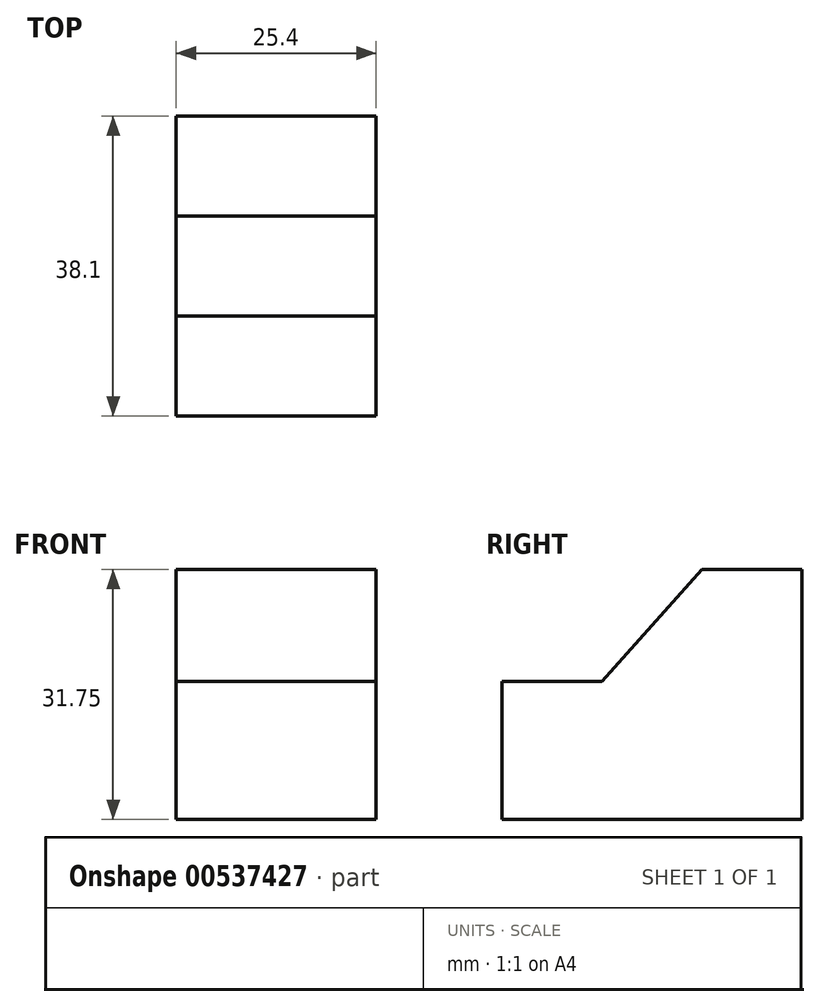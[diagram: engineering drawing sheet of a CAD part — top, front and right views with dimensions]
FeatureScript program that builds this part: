
annotation { "Feature Type Name" : "Feature", "Feature Type Description" : "" }
export const myFeature = defineFeature(function(context is Context, id is Id, definition is map)
    precondition{}
    {
        {
            var Q0;
            Q0=qCreatedBy(makeId("Top.planeOp"),FACE);
            var sketch = newSketch(context, id + "F0", { "sketchPlane" : qUnion([Q0])});
            skLineSegment(sketch, "E0", {"start": v(0, 0) * mm, "end": v(0, 38.1) * mm});
            skLineSegment(sketch, "E1", {"start": v(0, 38.1) * mm, "end": v(25.4, 38.1) * mm});
            skLineSegment(sketch, "E2", {"start": v(25.4, 38.1) * mm, "end": v(25.4, 0) * mm});
            skLineSegment(sketch, "E3", {"start": v(25.4, 0) * mm, "end": v(0, 0) * mm});
            skSolve(sketch);
        }
        {
            var Q0;
            Q0 = qSketchRegion(id + "F0", true);
            var Q1;
            Q1=makeQuery(id+"F0.imprint","IMPRINT",FACE,{"disambiguationData":[TD([[makeQuery(id+"F0.imprint","IMPRINT",EDGE,{"derivedFrom":sQuery(id+"F0.wireOp",EDGE,"E0")}),-1.0]])]});
            extrude(context, id + "F1", {"entities" : qUnion([Q0, Q1]), "depth" : 31.75 * mm, "offsetDistance" : 25.4 * mm});
        }
        {
            var Q0;
            Q0=makeQuery(id+"F1.opExtrude","SWEPT_FACE",FACE,{"disambiguationData":[OSD([sQuery(id+"F0.wireOp",EDGE,"E0")])]});
            var sketch = newSketch(context, id + "F2", { "sketchPlane" : qUnion([Q0])});
            skLineSegment(sketch, "E4", {"start": v(-25.4, 31.75) * mm, "end": v(-12.7, 17.55) * mm});
            skLineSegment(sketch, "E5", {"start": v(-12.7, 17.55) * mm, "end": v(0, 17.55) * mm});
            skLineSegment(sketch, "E6", {"start": v(0, 17.55) * mm, "end": v(0, 31.75) * mm});
            skLineSegment(sketch, "E7", {"start": v(0, 31.75) * mm, "end": v(-25.4, 31.75) * mm});
            skSolve(sketch);
        }
        {
            var Q0;
            Q0=makeQuery(id+"F2.imprint","IMPRINT",FACE,{"disambiguationData":[TD([[makeQuery(id+"F2.imprint","IMPRINT",EDGE,{"derivedFrom":sQuery(id+"F2.wireOp",EDGE,"E4")}),1.0]])]});
            extrude(context, id + "F3", {"entities" : qUnion([Q0]), "operationType" : NewBodyOperationType.REMOVE, "oppositeDirection" : true, "depth" : 25.4 * mm, "offsetDistance" : 25.4 * mm});
        }
    });
